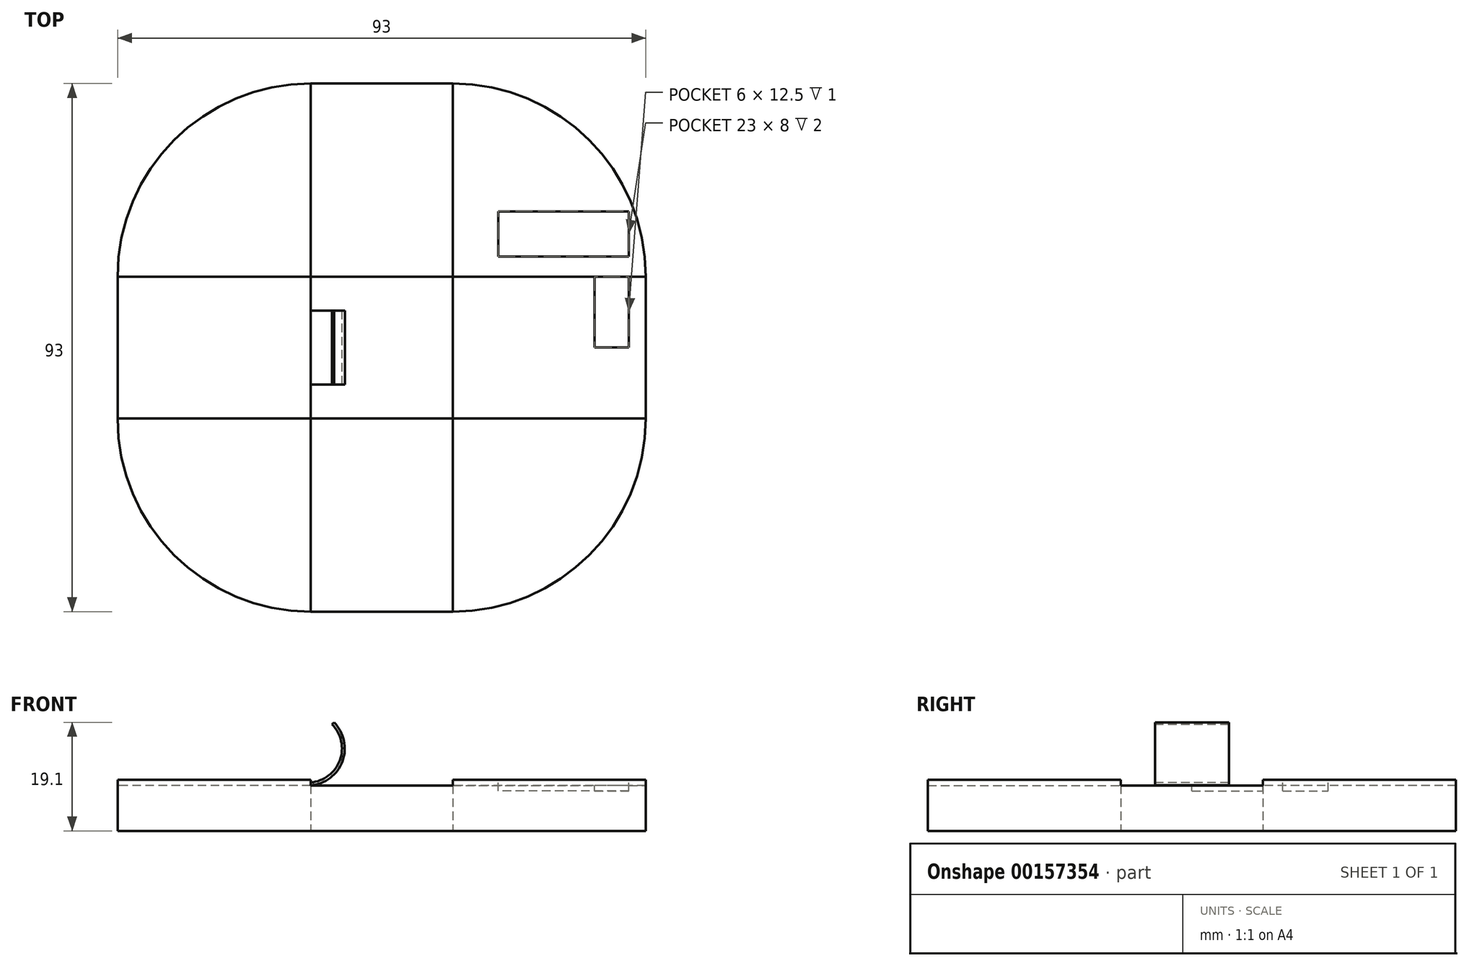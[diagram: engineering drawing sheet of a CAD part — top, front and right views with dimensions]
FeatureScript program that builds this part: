
annotation { "Feature Type Name" : "Feature", "Feature Type Description" : "" }
export const myFeature = defineFeature(function(context is Context, id is Id, definition is map)
    precondition{}
    {
        {
            var Q0;
            Q0=qCreatedBy(makeId("Top.planeOp"),FACE);
            var sketch = newSketch(context, id + "F0", { "sketchPlane" : qUnion([Q0])});
            skLineSegment(sketch, "E0.bottom", {"start": v(-12.5, 46.5) * mm, "end": v(12.5, 46.5) * mm});
            skLineSegment(sketch, "E0.top", {"start": v(-12.5, 12.5) * mm, "end": v(12.5, 12.5) * mm});
            skLineSegment(sketch, "E0.left", {"start": v(-12.5, 46.5) * mm, "end": v(-12.5, 12.5) * mm});
            skLineSegment(sketch, "E0.right", {"start": v(12.5, 46.5) * mm, "end": v(12.5, 12.5) * mm});
            skLineSegment(sketch, "E1.1.0", {"start": v(-46.5, -12.5) * mm, "end": v(-12.5, -12.5) * mm});
            skLineSegment(sketch, "E1.1.1", {"start": v(-46.5, -12.5) * mm, "end": v(-46.5, 12.5) * mm});
            skLineSegment(sketch, "E1.1.2", {"start": v(-46.5, 12.5) * mm, "end": v(-12.5, 12.5) * mm});
            skLineSegment(sketch, "E1.1.3", {"start": v(-12.5, -12.5) * mm, "end": v(-12.5, 12.5) * mm});
            skLineSegment(sketch, "E1.2.0", {"start": v(12.5, -46.5) * mm, "end": v(12.5, -12.5) * mm});
            skLineSegment(sketch, "E1.2.1", {"start": v(12.5, -46.5) * mm, "end": v(-12.5, -46.5) * mm});
            skLineSegment(sketch, "E1.2.2", {"start": v(-12.5, -46.5) * mm, "end": v(-12.5, -12.5) * mm});
            skLineSegment(sketch, "E1.2.3", {"start": v(12.5, -12.5) * mm, "end": v(-12.5, -12.5) * mm});
            skLineSegment(sketch, "E1.3.0", {"start": v(46.5, 12.5) * mm, "end": v(12.5, 12.5) * mm});
            skLineSegment(sketch, "E1.3.1", {"start": v(46.5, 12.5) * mm, "end": v(46.5, -12.5) * mm});
            skLineSegment(sketch, "E1.3.2", {"start": v(46.5, -12.5) * mm, "end": v(12.5, -12.5) * mm});
            skLineSegment(sketch, "E1.3.3", {"start": v(12.5, 12.5) * mm, "end": v(12.5, -12.5) * mm});
            skPoint(sketch, "E1.center", {"position": v(0, 0) * mm});
            skArc(sketch, "E2", {"start": v(-12.5, 46.5) * mm, "mid": v(-36.54, 36.54) * mm, "end": v(-46.5, 12.5) * mm});
            skArc(sketch, "E3", {"start": v(46.5, 12.5) * mm, "mid": v(36.54, 36.54) * mm, "end": v(12.5, 46.5) * mm});
            skArc(sketch, "E4", {"start": v(12.5, -46.5) * mm, "mid": v(36.54, -36.54) * mm, "end": v(46.5, -12.5) * mm});
            skArc(sketch, "E5", {"start": v(-46.5, -12.5) * mm, "mid": v(-36.54, -36.54) * mm, "end": v(-12.5, -46.5) * mm});
            skSolve(sketch);
        }
        {
            var Q0;
            Q0=makeQuery(id+"F0.imprint","IMPRINT",FACE,{"disambiguationData":[TD([[makeQuery(id+"F0.imprint","IMPRINT",EDGE,{"derivedFrom":sQuery(id+"F0.wireOp",EDGE,"E1.1.0")}),1.0]])]});
            var Q1;
            Q1=makeQuery(id+"F0.imprint","IMPRINT",FACE,{"disambiguationData":[TD([[makeQuery(id+"F0.imprint","IMPRINT",EDGE,{"derivedFrom":sQuery(id+"F0.wireOp",EDGE,"E1.2.0")}),1.0]])]});
            var Q2;
            Q2=makeQuery(id+"F0.imprint","IMPRINT",FACE,{"disambiguationData":[TD([[makeQuery(id+"F0.imprint","IMPRINT",EDGE,{"derivedFrom":sQuery(id+"F0.wireOp",EDGE,"E1.3.0")}),1.0]])]});
            var Q3;
            Q3=makeQuery(id+"F0.imprint","IMPRINT",FACE,{"disambiguationData":[TD([[makeQuery(id+"F0.imprint","IMPRINT",EDGE,{"derivedFrom":sQuery(id+"F0.wireOp",EDGE,"E0.bottom")}),-1.0]])]});
            var Q4;
            Q4=makeQuery(id+"F0.imprint","IMPRINT",FACE,{"disambiguationData":[TD([[makeQuery(id+"F0.imprint","IMPRINT",EDGE,{"derivedFrom":sQuery(id+"F0.wireOp",EDGE,"E0.left")}),-1.0]])]});
            var Q5;
            Q5=makeQuery(id+"F0.imprint","IMPRINT",FACE,{"disambiguationData":[TD([[makeQuery(id+"F0.imprint","IMPRINT",EDGE,{"derivedFrom":sQuery(id+"F0.wireOp",EDGE,"E0.right")}),1.0]])]});
            var Q6;
            Q6=makeQuery(id+"F0.imprint","IMPRINT",FACE,{"disambiguationData":[TD([[makeQuery(id+"F0.imprint","IMPRINT",EDGE,{"derivedFrom":sQuery(id+"F0.wireOp",EDGE,"E1.2.0")}),-1.0]])]});
            var Q7;
            Q7=makeQuery(id+"F0.imprint","IMPRINT",FACE,{"disambiguationData":[TD([[makeQuery(id+"F0.imprint","IMPRINT",EDGE,{"derivedFrom":sQuery(id+"F0.wireOp",EDGE,"E1.1.0")}),-1.0]])]});
            extrude(context, id + "F1", {"entities" : qUnion([Q0, Q1, Q2, Q3, Q4, Q5, Q6, Q7]), "depth" : 9 * mm});
        }
        {
            var Q0;
            Q0=makeQuery(id+"F1.opExtrude","CAP_FACE",FACE,{"disambiguationData":[OSD([sQuery(id+"F0.wireOp",EDGE,"E0.bottom"),sQuery(id+"F0.wireOp",EDGE,"E0.top"),sQuery(id+"F0.wireOp",EDGE,"E1.1.1"),sQuery(id+"F0.wireOp",EDGE,"E1.1.3"),sQuery(id+"F0.wireOp",EDGE,"E1.2.1"),sQuery(id+"F0.wireOp",EDGE,"E1.2.3"),sQuery(id+"F0.wireOp",EDGE,"E1.3.1"),sQuery(id+"F0.wireOp",EDGE,"E1.3.3"),sQuery(id+"F0.wireOp",EDGE,"E2"),sQuery(id+"F0.wireOp",EDGE,"E3"),sQuery(id+"F0.wireOp",EDGE,"E4"),sQuery(id+"F0.wireOp",EDGE,"E5")])],"isStart":false});
            var sketch = newSketch(context, id + "F2", { "sketchPlane" : qUnion([Q0])});
            skLineSegment(sketch, "E6.0.0", {"start": v(-46.5, 12.5) * mm, "end": v(-46.5, -12.5) * mm});
            skArc(sketch, "E6.0.1", {"start": v(-46.5, -12.5) * mm, "mid": v(-36.54, -36.54) * mm, "end": v(-12.5, -46.5) * mm});
            skLineSegment(sketch, "E6.0.2", {"start": v(-12.5, -46.5) * mm, "end": v(12.5, -46.5) * mm});
            skArc(sketch, "E6.0.3", {"start": v(12.5, -46.5) * mm, "mid": v(36.54, -36.54) * mm, "end": v(46.5, -12.5) * mm});
            skLineSegment(sketch, "E6.0.4", {"start": v(46.5, -12.5) * mm, "end": v(46.5, 12.5) * mm});
            skArc(sketch, "E6.0.5", {"start": v(46.5, 12.5) * mm, "mid": v(36.54, 36.54) * mm, "end": v(12.5, 46.5) * mm});
            skLineSegment(sketch, "E6.0.6", {"start": v(12.5, 46.5) * mm, "end": v(-12.5, 46.5) * mm});
            skArc(sketch, "E6.0.7", {"start": v(-12.5, 46.5) * mm, "mid": v(-36.54, 36.54) * mm, "end": v(-46.5, 12.5) * mm});
            skLineSegment(sketch, "E7", {"start": v(-46.5, 12.5) * mm, "end": v(46.5, 12.5) * mm});
            skLineSegment(sketch, "E8", {"start": v(46.5, -12.5) * mm, "end": v(-46.5, -12.5) * mm});
            skLineSegment(sketch, "E9", {"start": v(-12.5, 46.5) * mm, "end": v(-12.5, -46.5) * mm});
            skLineSegment(sketch, "E10", {"start": v(12.5, -46.5) * mm, "end": v(12.5, 46.5) * mm});
            skSolve(sketch);
        }
        {
            var Q0;
            {var subQ0=sQuery(id+"F2.wireOp",EDGE,"E6.0.0");Q0=makeQuery(id+"F2.imprint","IMPRINT",FACE,{"disambiguationData":[TD([[makeQuery(id+"F2.imprint","IMPRINT",EDGE,{"derivedFrom":subQ0}),-1.0]])]});}
            var Q1;
            {var subQ0=sQuery(id+"F2.wireOp",EDGE,"E6.0.2");Q1=makeQuery(id+"F2.imprint","IMPRINT",FACE,{"disambiguationData":[TD([[makeQuery(id+"F2.imprint","IMPRINT",EDGE,{"derivedFrom":subQ0}),-1.0]])]});}
            var Q2;
            {var subQ0=sQuery(id+"F2.wireOp",EDGE,"E6.0.4");Q2=makeQuery(id+"F2.imprint","IMPRINT",FACE,{"disambiguationData":[TD([[makeQuery(id+"F2.imprint","IMPRINT",EDGE,{"derivedFrom":subQ0}),-1.0]])]});}
            var Q3;
            {var subQ0=sQuery(id+"F2.wireOp",EDGE,"E6.0.6");Q3=makeQuery(id+"F2.imprint","IMPRINT",FACE,{"disambiguationData":[TD([[makeQuery(id+"F2.imprint","IMPRINT",EDGE,{"derivedFrom":subQ0}),-1.0]])]});}
            extrude(context, id + "F3", {"entities" : qUnion([Q0, Q1, Q2, Q3]), "operationType" : NewBodyOperationType.REMOVE, "oppositeDirection" : true, "depth" : 1 * mm});
        }
        {
            var Q0;
            Q0=qCreatedBy(makeId("Front.planeOp"),FACE);
            var sketch = newSketch(context, id + "F4", { "sketchPlane" : qUnion([Q0])});
            skLineSegment(sketch, "E11.0.0", {"start": v(-46.5, 0) * mm, "end": v(-12.5, 0) * mm});
            skLineSegment(sketch, "E11.0.1", {"start": v(-12.5, 0) * mm, "end": v(-12.5, 8) * mm});
            skLineSegment(sketch, "E11.0.2", {"start": v(-12.5, 8) * mm, "end": v(-12.5, 9) * mm});
            skLineSegment(sketch, "E11.0.3", {"start": v(-12.5, 9) * mm, "end": v(-46.5, 9) * mm});
            skLineSegment(sketch, "E11.0.4", {"start": v(-46.5, 9) * mm, "end": v(-46.5, 8) * mm});
            skLineSegment(sketch, "E11.0.5", {"start": v(-46.5, 8) * mm, "end": v(-46.5, 0) * mm});
            skLineSegment(sketch, "E12", {"start": v(-12.5, 8) * mm, "end": v(-28.18, 8) * mm});
            skPoint(sketch, "E13", {"position": v(-13, 14.5) * mm});
            skCircle(sketch, "E14", {"center": v(-13, 14.5) * mm, "radius": 6.5 * mm});
            skCircle(sketch, "E15", {"center": v(-13, 14.5) * mm, "radius": 6 * mm});
            skLineSegment(sketch, "E16", {"start": v(-12.5, 8) * mm, "end": v(-12.5, 8.5) * mm});
            skLineSegment(sketch, "E17", {"start": v(-13, 14.5) * mm, "end": v(-13, 20.5) * mm});
            skLineSegment(sketch, "E18", {"start": v(-13, 14.5) * mm, "end": v(-8.76, 18.74) * mm});
            skLineSegment(sketch, "E19", {"start": v(-8.76, 18.74) * mm, "end": v(-8.4, 19.1) * mm});
            skSolve(sketch);
        }
        {
            var Q0;
            {var subQ5=sQuery(id+"F4.wireOp",EDGE,"E19");Q0=makeQuery(id+"F4.imprint","IMPRINT",FACE,{"disambiguationData":[TD([[makeQuery(id+"F4.imprint","IMPRINT",EDGE,{"derivedFrom":subQ5}),-1.0]])]});}
            extrude(context, id + "F5", {"entities" : qUnion([Q0]), "endBound" : BoundingType.SYMMETRIC, "depth" : 13 * mm});
        }
        {
            var Q0;
            Q0=qCreatedBy(makeId("Front.planeOp"),FACE);
            var sketch = newSketch(context, id + "F6", { "sketchPlane" : qUnion([Q0])});
            skLineSegment(sketch, "E20.0.0", {"start": v(12.5, 0) * mm, "end": v(12.5, 8) * mm});
            skLineSegment(sketch, "E20.0.1", {"start": v(12.5, 8) * mm, "end": v(-12.5, 8) * mm});
            skLineSegment(sketch, "E20.0.2", {"start": v(-12.5, 8) * mm, "end": v(-12.5, 0) * mm});
            skLineSegment(sketch, "E20.0.3", {"start": v(-12.5, 0) * mm, "end": v(12.5, 0) * mm});
            skLineSegment(sketch, "E21", {"start": v(0, 0) * mm, "end": v(0, 23.72) * mm});
            skPoint(sketch, "E21.endSnap0", {"position": v(0, 8) * mm});
            skSolve(sketch);
        }
        {
            var Q0;
            {var subQ4=sQuery(id+"F0.wireOp",EDGE,"E3");var subQ5=sQuery(id+"F0.wireOp",EDGE,"E1.3.3");Q0=makeQuery(id+"F3.boolean.opBoolean","SPLIT",FACE,{"disambiguationData":[TD([makeQuery(id+"F1.opExtrude","SWEPT_FACE",FACE,{"disambiguationData":[OSD([subQ4])]})])],"derivedFrom":makeQuery(id+"F1.opExtrude","CAP_FACE",FACE,{"disambiguationData":[OSD([sQuery(id+"F0.wireOp",EDGE,"E0.bottom"),sQuery(id+"F0.wireOp",EDGE,"E0.top"),sQuery(id+"F0.wireOp",EDGE,"E1.1.1"),sQuery(id+"F0.wireOp",EDGE,"E1.1.3"),sQuery(id+"F0.wireOp",EDGE,"E1.2.1"),sQuery(id+"F0.wireOp",EDGE,"E1.2.3"),sQuery(id+"F0.wireOp",EDGE,"E1.3.1"),subQ5,sQuery(id+"F0.wireOp",EDGE,"E2"),subQ4,sQuery(id+"F0.wireOp",EDGE,"E4"),sQuery(id+"F0.wireOp",EDGE,"E5")])],"isStart":false})});}
            var sketch = newSketch(context, id + "F7", { "sketchPlane" : qUnion([Q0])});
            skLineSegment(sketch, "E22.0.0", {"start": v(12.5, 46.5) * mm, "end": v(12.5, 12.5) * mm});
            skLineSegment(sketch, "E22.0.1", {"start": v(12.5, 12.5) * mm, "end": v(46.5, 12.5) * mm});
            skArc(sketch, "E22.0.2", {"start": v(46.5, 12.5) * mm, "mid": v(36.54, 36.54) * mm, "end": v(12.5, 46.5) * mm});
            skLineSegment(sketch, "E23.0.0", {"start": v(46.5, 12.5) * mm, "end": v(12.5, 12.5) * mm});
            skLineSegment(sketch, "E23.0.1", {"start": v(12.5, 12.5) * mm, "end": v(12.5, -12.5) * mm});
            skLineSegment(sketch, "E23.0.2", {"start": v(12.5, -12.5) * mm, "end": v(46.5, -12.5) * mm});
            skLineSegment(sketch, "E23.0.3", {"start": v(46.5, -12.5) * mm, "end": v(46.5, 12.5) * mm});
            skLineSegment(sketch, "E24.bottom", {"start": v(43.5, 0) * mm, "end": v(37.5, 0) * mm});
            skLineSegment(sketch, "E24.top", {"start": v(43.5, 16) * mm, "end": v(37.5, 16) * mm});
            skLineSegment(sketch, "E24.left", {"start": v(43.5, 0) * mm, "end": v(43.5, 16) * mm});
            skLineSegment(sketch, "E24.right", {"start": v(37.5, 0) * mm, "end": v(37.5, 16) * mm});
            skLineSegment(sketch, "E25.bottom", {"start": v(43.5, 16) * mm, "end": v(20.5, 16) * mm});
            skLineSegment(sketch, "E25.top", {"start": v(43.5, 24) * mm, "end": v(20.5, 24) * mm});
            skLineSegment(sketch, "E25.left", {"start": v(43.5, 16) * mm, "end": v(43.5, 24) * mm});
            skLineSegment(sketch, "E25.right", {"start": v(20.5, 16) * mm, "end": v(20.5, 24) * mm});
            skSolve(sketch);
        }
        {
            var Q0;
            Q0=makeQuery(id+"F7.imprint","IMPRINT",FACE,{"disambiguationData":[TD([[makeQuery(id+"F7.imprint","IMPRINT",EDGE,{"derivedFrom":sQuery(id+"F7.wireOp",EDGE,"E25.top")}),1.0]])]});
            var Q1;
            {var subQ5=sQuery(id+"F7.wireOp",EDGE,"E24.bottom");Q1=makeQuery(id+"F7.imprint","IMPRINT",FACE,{"disambiguationData":[TD([[makeQuery(id+"F7.imprint","IMPRINT",EDGE,{"derivedFrom":subQ5}),-1.0]])]});}
            var Q2;
            {var subQ0=sQuery(id+"F7.wireOp",EDGE,"E24.right");var subQ1=sQuery(id+"F7.wireOp",EDGE,"E23.0.0");var subQ2=makeQuery(id+"F7.imprint","INTERSECT",VERTEX,{"derivedFrom":[subQ1,subQ0]});Q2=makeQuery(id+"F7.imprint","IMPRINT",FACE,{"disambiguationData":[TD([[makeQuery(id+"F7.imprint","IMPRINT",EDGE,{"disambiguationData":[TD([[subQ2,-1.0]])],"derivedFrom":subQ1}),1.0]])]});}
            extrude(context, id + "F8", {"entities" : qUnion([Q0, Q1, Q2]), "operationType" : NewBodyOperationType.REMOVE, "oppositeDirection" : true, "depth" : 2 * mm});
        }
    });
